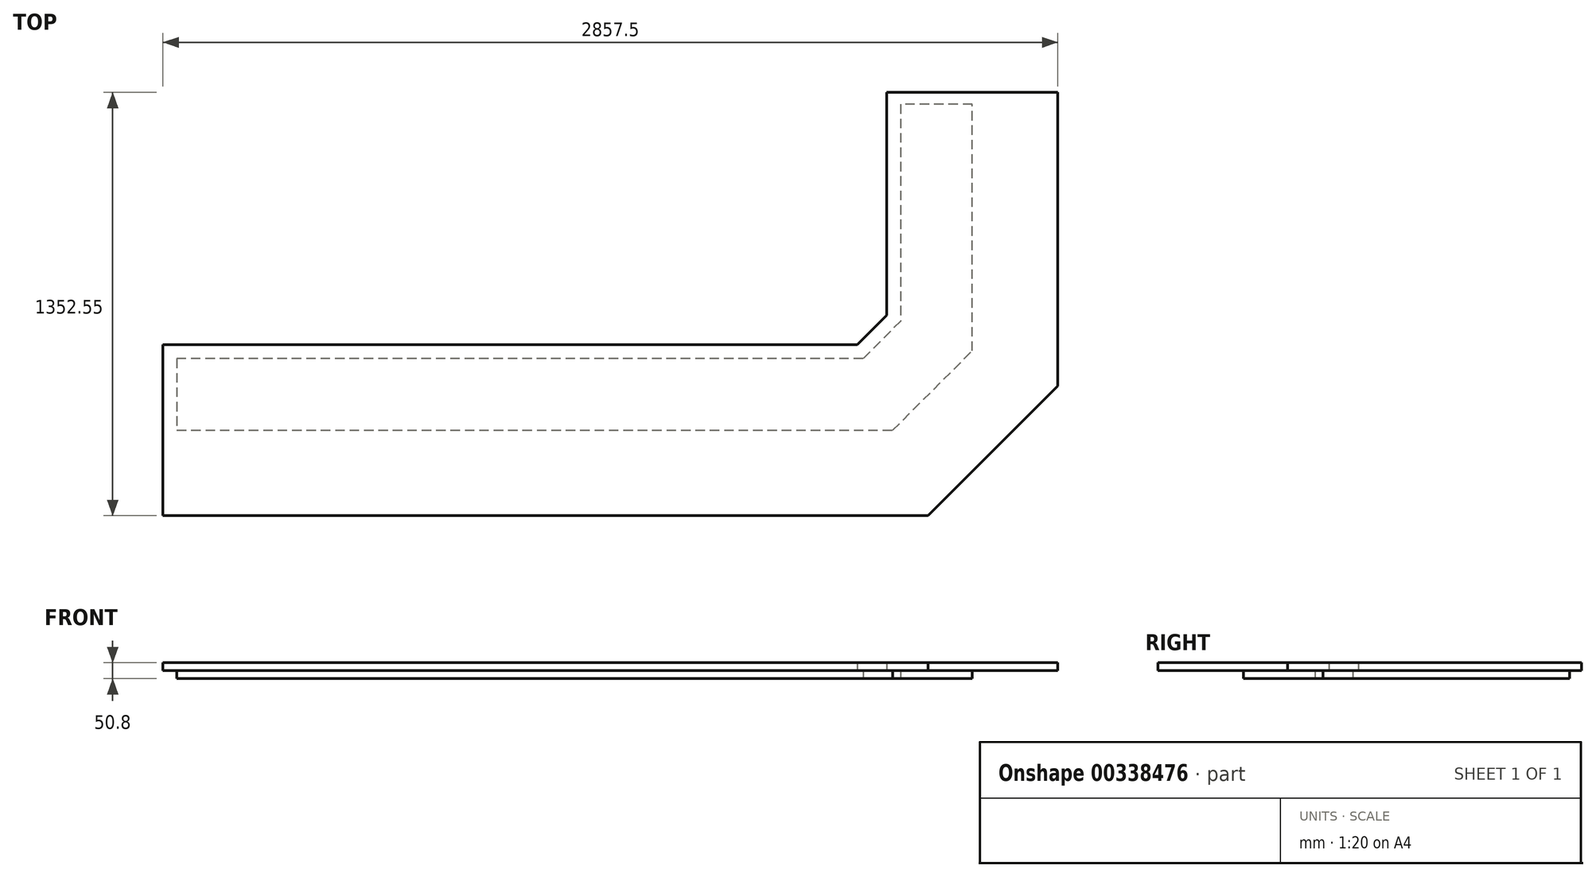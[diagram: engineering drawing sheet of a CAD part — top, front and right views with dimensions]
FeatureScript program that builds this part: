
annotation { "Feature Type Name" : "Feature", "Feature Type Description" : "" }
export const myFeature = defineFeature(function(context is Context, id is Id, definition is map)
    precondition{}
    {
        {
            var Q0;
            Q0=qCreatedBy(makeId("Top.planeOp"),FACE);
            var sketch = newSketch(context, id + "F0", { "sketchPlane" : qUnion([Q0])});
            skLineSegment(sketch, "E0", {"start": v(-2540, -486.9) * mm, "end": v(-254, -486.9) * mm});
            skLineSegment(sketch, "E1", {"start": v(-254, -486.9) * mm, "end": v(0, -232.9) * mm});
            skLineSegment(sketch, "E2", {"start": v(0, -232.9) * mm, "end": v(0, 554.5) * mm});
            skLineSegment(sketch, "E3", {"start": v(0, 554.5) * mm, "end": v(-228.6, 554.5) * mm});
            skLineSegment(sketch, "E4", {"start": v(-228.6, 554.5) * mm, "end": v(-228.6, -138.2) * mm});
            skLineSegment(sketch, "E5", {"start": v(-228.6, -138.2) * mm, "end": v(-348.69, -258.3) * mm});
            skLineSegment(sketch, "E6", {"start": v(-348.69, -258.3) * mm, "end": v(-2540, -258.3) * mm});
            skLineSegment(sketch, "E7", {"start": v(-2540, -258.3) * mm, "end": v(-2540, -486.9) * mm});
            skLineSegment(sketch, "E8", {"start": v(-348.69, -258.3) * mm, "end": v(-254, -486.9) * mm, "construction": true});
            skLineSegment(sketch, "E9", {"start": v(-228.6, -138.2) * mm, "end": v(0, -232.9) * mm, "construction": true});
            skSolve(sketch);
        }
        {
            var Q0;
            Q0=makeQuery(id+"F0.imprint","IMPRINT",FACE,{"disambiguationData":[TD([[makeQuery(id+"F0.imprint","IMPRINT",EDGE,{"derivedFrom":sQuery(id+"F0.wireOp",EDGE,"E0")}),1.0]])]});
            extrude(context, id + "F1", {"entities" : qUnion([Q0]), "depth" : 25.4 * mm});
        }
        {
            var Q0;
            Q0=makeQuery(id+"F1.opExtrude","CAP_FACE",FACE,{"disambiguationData":[OSD([sQuery(id+"F0.wireOp",EDGE,"E0"),sQuery(id+"F0.wireOp",EDGE,"E1"),sQuery(id+"F0.wireOp",EDGE,"E2"),sQuery(id+"F0.wireOp",EDGE,"E3"),sQuery(id+"F0.wireOp",EDGE,"E4"),sQuery(id+"F0.wireOp",EDGE,"E5"),sQuery(id+"F0.wireOp",EDGE,"E6"),sQuery(id+"F0.wireOp",EDGE,"E7")])],"isStart":false});
            var sketch = newSketch(context, id + "F2", { "sketchPlane" : qUnion([Q0])});
            skLineSegment(sketch, "E10.0", {"start": v(-2540, -486.9) * mm, "end": v(-254, -486.9) * mm});
            skLineSegment(sketch, "E11.0", {"start": v(-348.69, -258.3) * mm, "end": v(-2540, -258.3) * mm});
            skPoint(sketch, "E12.0", {"position": v(-288.64, -198.25) * mm});
            skLineSegment(sketch, "E13.0", {"start": v(-228.6, 554.5) * mm, "end": v(-228.6, -138.2) * mm});
            skLineSegment(sketch, "E14.0", {"start": v(0, -232.9) * mm, "end": v(0, 554.5) * mm});
            skPoint(sketch, "E15.0", {"position": v(-127, -359.9) * mm});
            skLineSegment(sketch, "E16.0", {"start": v(-254, -486.9) * mm, "end": v(0, -232.9) * mm});
            skLineSegment(sketch, "E17.0", {"start": v(-228.6, -138.2) * mm, "end": v(-348.69, -258.3) * mm});
            skLineSegment(sketch, "E18.0", {"start": v(-2540, -258.3) * mm, "end": v(-2540, -486.9) * mm});
            skLineSegment(sketch, "E19", {"start": v(-2584.45, -213.85) * mm, "end": v(-2584.45, -759.95) * mm});
            skLineSegment(sketch, "E20", {"start": v(-2584.45, -759.95) * mm, "end": v(-140.9, -759.95) * mm});
            skLineSegment(sketch, "E21", {"start": v(-140.9, -759.95) * mm, "end": v(273.05, -346) * mm});
            skLineSegment(sketch, "E22", {"start": v(273.05, -346) * mm, "end": v(273.05, 592.6) * mm});
            skLineSegment(sketch, "E23", {"start": v(273.05, 592.6) * mm, "end": v(-273.05, 592.6) * mm});
            skLineSegment(sketch, "E24", {"start": v(-273.05, 592.6) * mm, "end": v(-273.05, -119.8) * mm});
            skLineSegment(sketch, "E25", {"start": v(-2584.45, -213.85) * mm, "end": v(-367.1, -213.85) * mm});
            skLineSegment(sketch, "E26", {"start": v(-367.1, -213.85) * mm, "end": v(-273.05, -119.8) * mm});
            skSolve(sketch);
        }
        {
            var Q0;
            Q0 = qSketchRegion(id + "F2", true);
            extrude(context, id + "F3", {"entities" : qUnion([Q0]), "operationType" : NewBodyOperationType.ADD, "depth" : 25.4 * mm});
        }
    });
